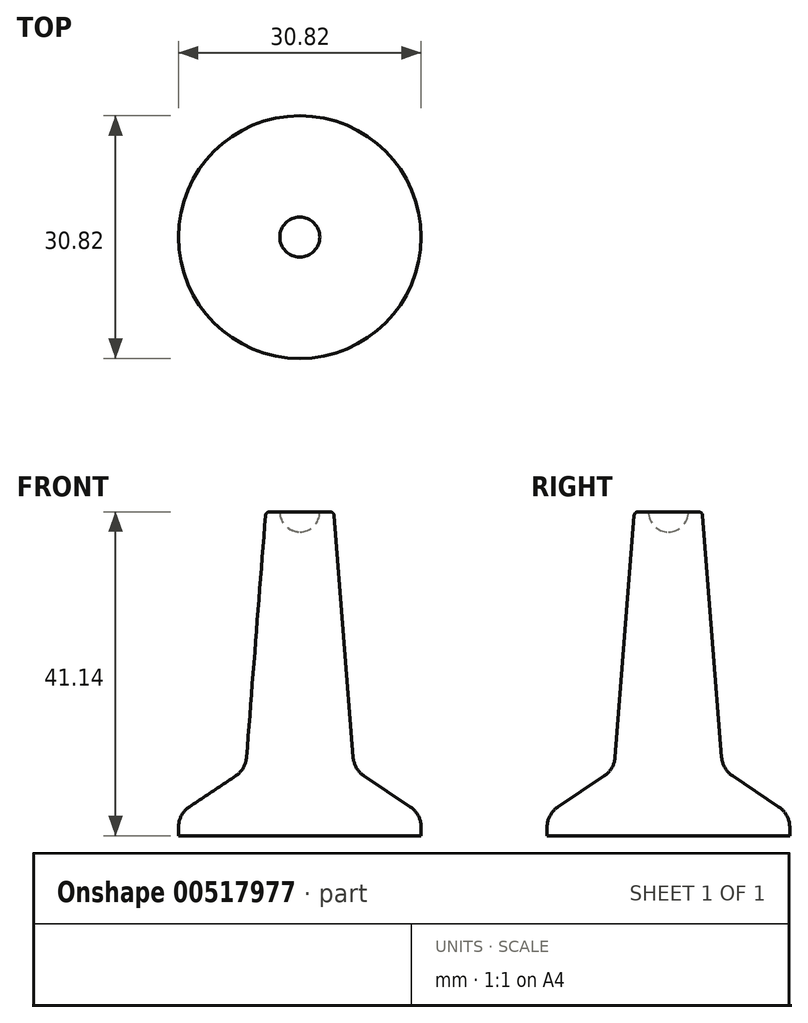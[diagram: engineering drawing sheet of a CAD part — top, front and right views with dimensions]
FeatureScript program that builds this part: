
annotation { "Feature Type Name" : "Feature", "Feature Type Description" : "" }
export const myFeature = defineFeature(function(context is Context, id is Id, definition is map)
    precondition{}
    {
        {
            var Q0;
            Q0=qCreatedBy(makeId("Front.planeOp"),FACE);
            var sketch = newSketch(context, id + "F0", { "sketchPlane" : qUnion([Q0])});
            skLineSegment(sketch, "E0", {"start": v(0, 21.84) * mm, "end": v(0, -21.84) * mm});
            skLineSegment(sketch, "E1", {"start": v(2.54, 19.3) * mm, "end": v(3.85, 19.3) * mm});
            skPoint(sketch, "E2.orphan", {"position": v(0, 19.3) * mm});
            skLineSegment(sketch, "E3", {"start": v(4.35, 18.84) * mm, "end": v(6.77, -11.87) * mm});
            skArc(sketch, "E4.filletArc", {"start": v(4.35, 18.84) * mm, "mid": v(4.2, 19.17) * mm, "end": v(3.85, 19.3) * mm});
            skLineSegment(sketch, "E5", {"start": v(8.18, -14.27) * mm, "end": v(14, -18.15) * mm});
            skLineSegment(sketch, "E6", {"start": v(15.41, -20.79) * mm, "end": v(15.41, -21.84) * mm});
            skLineSegment(sketch, "E7", {"start": v(15.41, -21.84) * mm, "end": v(0, -21.84) * mm});
            skPoint(sketch, "E8.visualSharp", {"position": v(6.9, -13.41) * mm});
            skArc(sketch, "E8.filletArc", {"start": v(6.77, -11.87) * mm, "mid": v(7.2, -13.23) * mm, "end": v(8.18, -14.27) * mm});
            skArc(sketch, "E9.filletArc", {"start": v(15.41, -20.79) * mm, "mid": v(15.04, -19.3) * mm, "end": v(14, -18.15) * mm});
            skLineSegment(sketch, "E10", {"start": v(0, -21.84) * mm, "end": v(0, 37.46) * mm, "construction": true});
            skArc(sketch, "E11", {"start": v(0, 16.76) * mm, "mid": v(1.8, 17.5) * mm, "end": v(2.54, 19.3) * mm});
            skSolve(sketch);
        }
        {
            var Q0;
            {var subQ2=sQuery(id+"F0.wireOp",EDGE,"E0");Q0=makeQuery(id+"F0.imprint","IMPRINT",FACE,{"disambiguationData":[TD([[makeQuery(id+"F0.imprint","IMPRINT",EDGE,{"derivedFrom":subQ2}),1.0]])]});}
            var Q1;
            Q1=sQuery(id+"F0.wireOp",EDGE,"E10");
            revolve(context, id + "F1", {"entities" : qUnion([Q0]), "axis" : qUnion([Q1]), "revolveType" : RevolveType.FULL});
        }
    });
